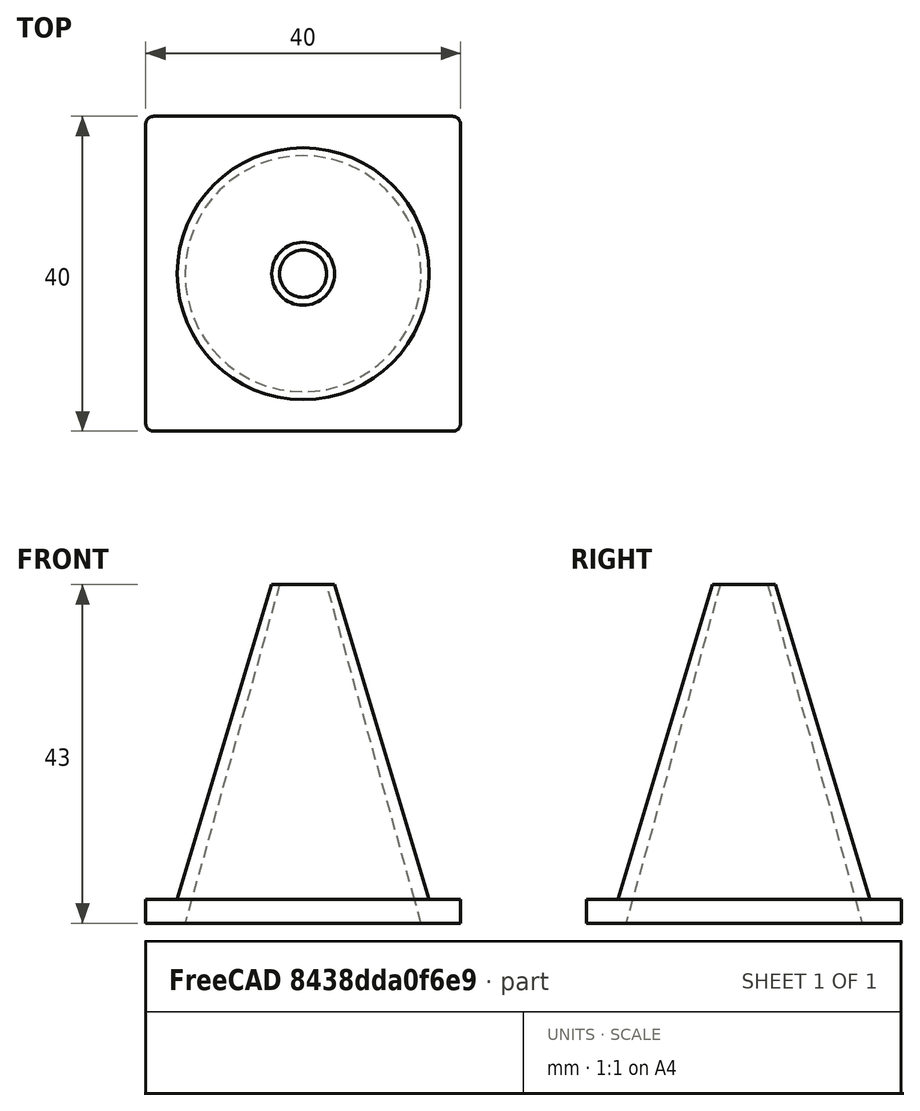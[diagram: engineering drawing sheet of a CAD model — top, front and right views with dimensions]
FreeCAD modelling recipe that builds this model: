
FCSTD DOCUMENT  (FreeCAD 1.0R39319 (Git))
Label: ojt1_t14r02_cone
License: All rights reserved
LicenseURL: https://en.wikipedia.org/wiki/All_rights_reserved
objects: Part::Cone×3, Part::Cut×2, Part::Box×1, Part::Fillet×1, Part::MultiFuse×1
note: 8 computed .brp shape members not serialized (recipe doc carries the construction recipe); baked Part::Feature solids carry a one-line shape summary decoded from their .brp

FEATURE [Part::Box] Box  label="Cube"
  AttacherType = Attacher::AttachEngine3D
  Height = 3
  Length = 40
  Width = 40
FEATURE [Part::Fillet] Fillet
  Base = -> Box
  EdgeLinks = -> Box [Edge1,Edge3,Edge5,Edge7]
  Edges = 4 edges r=1: [Edge1,Edge3,Edge5,Edge7]
FEATURE [Part::Cone] Cone
  Angle = 360
  AttacherType = Attacher::AttachEngine3D
  Height = 40
  Placement = pos=(20,20,3) rot=(0,0,1;0rad)
  Radius1 = 16
  Radius2 = 4
FEATURE [Part::Cone] Cone001
  Angle = 360
  AttacherType = Attacher::AttachEngine3D
  Height = 43
  Placement = pos=(20,20,0) rot=(0,0,1;0rad)
  Radius1 = 15
  Radius2 = 3
FEATURE [Part::Cone] Cone002
  Angle = 360
  AttacherType = Attacher::AttachEngine3D
  Height = 43
  Placement = pos=(20,20,0) rot=(0,0,1;0rad)
  Radius1 = 15
  Radius2 = 3
FEATURE [Part::Cut] Cut
  Base = -> Cone
  Refine = true
  Tool = -> Cone001
FEATURE [Part::Cut] Cut001
  Base = -> Fillet
  Refine = true
  Tool = -> Cone002
FEATURE [Part::MultiFuse] Fusion
  Refine = true
  Shapes = -> [Cut001,Cut]
